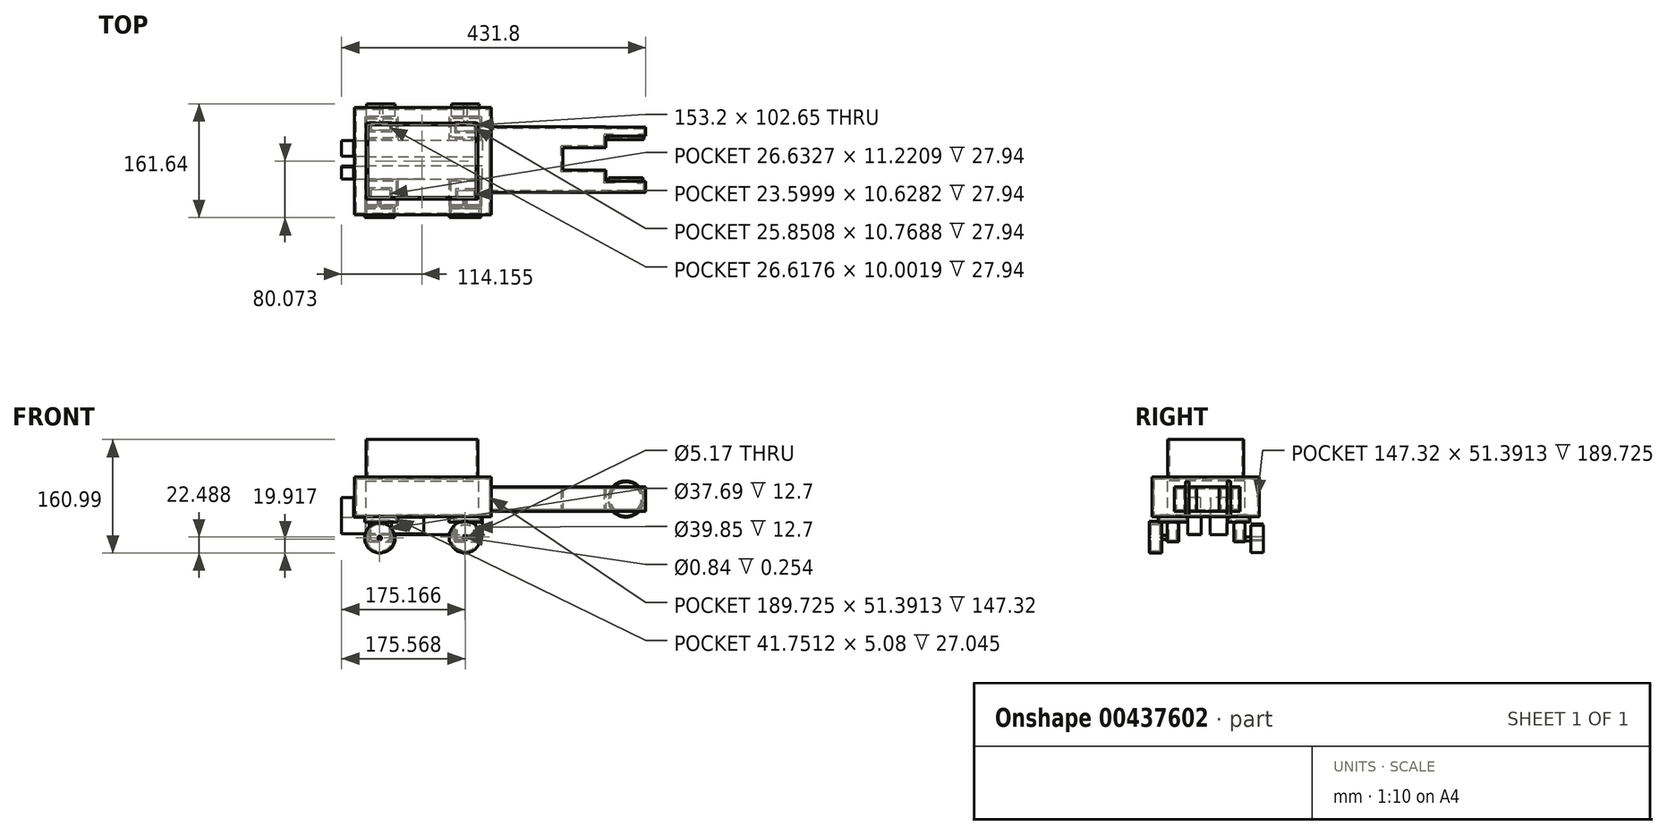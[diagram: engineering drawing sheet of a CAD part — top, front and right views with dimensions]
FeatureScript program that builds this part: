
annotation { "Feature Type Name" : "Feature", "Feature Type Description" : "" }
export const myFeature = defineFeature(function(context is Context, id is Id, definition is map)
    precondition{}
    {
        {
            var Q0;
            Q0=qCreatedBy(makeId("Front.planeOp"),FACE);
            var sketch = newSketch(context, id + "F0", { "sketchPlane" : qUnion([Q0])});
            skLineSegment(sketch, "E0.bottom", {"start": v(-98.79, 0) * mm, "end": v(96.02, 0) * mm});
            skLineSegment(sketch, "E0.top", {"start": v(-98.79, -56.47) * mm, "end": v(96.02, -56.47) * mm});
            skLineSegment(sketch, "E0.left", {"start": v(-98.79, 0) * mm, "end": v(-98.79, -56.47) * mm});
            skLineSegment(sketch, "E0.right", {"start": v(96.02, 0) * mm, "end": v(96.02, -56.47) * mm});
            skSolve(sketch);
        }
        {
            var Q0;
            Q0 = qSketchRegion(id + "F0", true);
            extrude(context, id + "F1", {"entities" : qUnion([Q0]), "depth" : 76.2 * mm});
        }
        {
            var Q0;
            Q0=makeQuery(id+"F1.opExtrude","CAP_FACE",FACE,{"disambiguationData":[OSD([sQuery(id+"F0.wireOp",EDGE,"E0.bottom"),sQuery(id+"F0.wireOp",EDGE,"E0.top"),sQuery(id+"F0.wireOp",EDGE,"E0.left"),sQuery(id+"F0.wireOp",EDGE,"E0.right")])],"isStart":true});
            extrude(context, id + "F2", {"entities" : qUnion([Q0]), "operationType" : NewBodyOperationType.ADD, "depth" : 76.2 * mm});
        }
        {
            var Q0;
            {var subQ0=sQuery(id+"F0.wireOp",EDGE,"E0.top");Q0=makeQuery(id+"F2.boolean.opBoolean","MERGE",FACE,{"derivedFrom":[makeQuery(id+"F1.opExtrude","SWEPT_FACE",FACE,{"disambiguationData":[OSD([subQ0])]}),makeQuery(id+"F2.opExtrude","SWEPT_FACE",FACE,{"disambiguationData":[OSD([subQ0])]})]});}
            var sketch = newSketch(context, id + "F3", { "sketchPlane" : qUnion([Q0])});
            skSolve(sketch);
        }
        {
            var Q0;
            {var subQ0=sQuery(id+"F0.wireOp",EDGE,"E0.top");Q0=makeQuery(id+"F3.imprint","IMPRINT",FACE,{"disambiguationData":[TD([[makeQuery(id+"F3.imprint","IMPRINT",EDGE,{"derivedFrom":makeQuery(id+"F1.opExtrude","CAP_EDGE",EDGE,{"disambiguationData":[OSD([subQ0])],"isStart":false})}),-1.0]])]});}
            var sketch = newSketch(context, id + "F4", { "sketchPlane" : qUnion([Q0])});
            skLineSegment(sketch, "E1.bottom", {"start": v(81.5, -62.59) * mm, "end": v(35.53, -62.59) * mm});
            skLineSegment(sketch, "E1.top", {"start": v(81.5, -30.8) * mm, "end": v(35.53, -30.8) * mm});
            skLineSegment(sketch, "E1.left", {"start": v(81.5, -62.59) * mm, "end": v(81.5, -30.8) * mm});
            skLineSegment(sketch, "E1.right", {"start": v(35.53, -62.59) * mm, "end": v(35.53, -30.8) * mm});
            skLineSegment(sketch, "E2.bottom", {"start": v(-83.86, -62.59) * mm, "end": v(-37.03, -62.59) * mm});
            skLineSegment(sketch, "E2.top", {"start": v(-83.86, -30.8) * mm, "end": v(-37.03, -30.8) * mm});
            skLineSegment(sketch, "E2.left", {"start": v(-83.86, -62.59) * mm, "end": v(-83.86, -30.8) * mm});
            skLineSegment(sketch, "E2.right", {"start": v(-37.03, -62.59) * mm, "end": v(-37.03, -30.8) * mm});
            skLineSegment(sketch, "E3.bottom", {"start": v(-83.86, 25.2) * mm, "end": v(-37.03, 25.2) * mm});
            skLineSegment(sketch, "E3.top", {"start": v(-83.86, 67.3) * mm, "end": v(-37.03, 67.3) * mm});
            skLineSegment(sketch, "E3.left", {"start": v(-83.86, 25.2) * mm, "end": v(-83.86, 67.3) * mm});
            skLineSegment(sketch, "E3.right", {"start": v(-37.03, 25.2) * mm, "end": v(-37.03, 67.3) * mm});
            skLineSegment(sketch, "E4.bottom", {"start": v(35.53, 25.2) * mm, "end": v(81.5, 25.2) * mm});
            skLineSegment(sketch, "E4.top", {"start": v(35.53, 67.3) * mm, "end": v(81.5, 67.3) * mm});
            skLineSegment(sketch, "E4.left", {"start": v(35.53, 25.2) * mm, "end": v(35.53, 67.3) * mm});
            skLineSegment(sketch, "E4.right", {"start": v(81.5, 25.2) * mm, "end": v(81.5, 67.3) * mm});
            skSolve(sketch);
        }
        {
            var Q0;
            Q0 = qSketchRegion(id + "F4", true);
            extrude(context, id + "F5", {"entities" : qUnion([Q0]), "operationType" : NewBodyOperationType.ADD, "depth" : 7.62 * mm});
        }
        {
            var Q0;
            {var subQ0=sQuery(id+"F0.wireOp",EDGE,"E0.top");Q0=makeQuery(id+"F3.imprint","IMPRINT",FACE,{"disambiguationData":[TD([[makeQuery(id+"F3.imprint","IMPRINT",EDGE,{"derivedFrom":makeQuery(id+"F1.opExtrude","CAP_EDGE",EDGE,{"disambiguationData":[OSD([subQ0])],"isStart":false})}),-1.0]])]});}
            var sketch = newSketch(context, id + "F6", { "sketchPlane" : qUnion([Q0])});
            skLineSegment(sketch, "E5.bottom", {"start": v(-77.55, 54.61) * mm, "end": v(-45.84, 54.61) * mm});
            skLineSegment(sketch, "E5.top", {"start": v(-77.55, 38.31) * mm, "end": v(-45.84, 38.31) * mm});
            skLineSegment(sketch, "E5.left", {"start": v(-77.55, 54.61) * mm, "end": v(-77.55, 38.31) * mm});
            skLineSegment(sketch, "E5.right", {"start": v(-45.84, 54.61) * mm, "end": v(-45.84, 38.31) * mm});
            skLineSegment(sketch, "E6.bottom", {"start": v(44.62, 54.91) * mm, "end": v(73.3, 54.91) * mm});
            skLineSegment(sketch, "E6.top", {"start": v(44.62, 39.2) * mm, "end": v(73.3, 39.2) * mm});
            skLineSegment(sketch, "E6.left", {"start": v(44.62, 54.91) * mm, "end": v(44.62, 39.2) * mm});
            skLineSegment(sketch, "E6.right", {"start": v(73.3, 54.91) * mm, "end": v(73.3, 39.2) * mm});
            skLineSegment(sketch, "E7.bottom", {"start": v(43.35, -39.87) * mm, "end": v(74.28, -39.87) * mm});
            skLineSegment(sketch, "E7.top", {"start": v(43.35, -55.72) * mm, "end": v(74.28, -55.72) * mm});
            skLineSegment(sketch, "E7.left", {"start": v(43.35, -39.87) * mm, "end": v(43.35, -55.72) * mm});
            skLineSegment(sketch, "E7.right", {"start": v(74.28, -39.87) * mm, "end": v(74.28, -55.72) * mm});
            skLineSegment(sketch, "E8.bottom", {"start": v(-77.57, -40.9) * mm, "end": v(-45.87, -40.9) * mm});
            skLineSegment(sketch, "E8.top", {"start": v(-77.57, -55.97) * mm, "end": v(-45.87, -55.97) * mm});
            skLineSegment(sketch, "E8.left", {"start": v(-77.57, -40.9) * mm, "end": v(-77.57, -55.97) * mm});
            skLineSegment(sketch, "E8.right", {"start": v(-45.87, -40.9) * mm, "end": v(-45.87, -55.97) * mm});
            skSolve(sketch);
        }
        {
            var Q0;
            Q0 = qSketchRegion(id + "F6", true);
            extrude(context, id + "F7", {"entities" : qUnion([Q0]), "operationType" : NewBodyOperationType.ADD, "depth" : 35.56 * mm});
        }
        {
            var Q0;
            Q0=makeQuery(id+"F7.opExtrude","SWEPT_FACE",FACE,{"disambiguationData":[OSD([sQuery(id+"F6.wireOp",EDGE,"E8.top")])]});
            var sketch = newSketch(context, id + "F8", { "sketchPlane" : qUnion([Q0])});
            skCircle(sketch, "E9", {"center": v(61, -87.01) * mm, "radius": 2.29 * mm});
            skPoint(sketch, "E9.first.point", {"position": v(59.2, -85.58) * mm});
            skPoint(sketch, "E9.second.point", {"position": v(62.7, -88.54) * mm});
            skPoint(sketch, "E9.third.point", {"position": v(60, -89.08) * mm});
            skCircle(sketch, "E10", {"center": v(-58.73, -87.73) * mm, "radius": 2.59 * mm});
            skPoint(sketch, "E10.first.point", {"position": v(-61.08, -86.66) * mm});
            skPoint(sketch, "E10.second.point", {"position": v(-56.52, -89.08) * mm});
            skPoint(sketch, "E10.third.point", {"position": v(-61.08, -88.8) * mm});
            skSolve(sketch);
        }
        {
            var Q0;
            Q0 = qSketchRegion(id + "F8", true);
            extrude(context, id + "F9", {"entities" : qUnion([Q0]), "operationType" : NewBodyOperationType.ADD, "depth" : 25.4 * mm});
        }
        {
            var Q0;
            Q0=makeQuery(id+"F9.opExtrude","CAP_FACE",FACE,{"disambiguationData":[OSD([sQuery(id+"F8.wireOp",EDGE,"E10")])],"isStart":false});
            var sketch = newSketch(context, id + "F10", { "sketchPlane" : qUnion([Q0])});
            skCircle(sketch, "E11", {"center": v(-58.73, -87.73) * mm, "radius": 19.64 * mm});
            skCircle(sketch, "E12", {"center": v(60.96, -86.76) * mm, "radius": 20.44 * mm});
            skSolve(sketch);
        }
        {
            var Q0;
            Q0=makeQuery(id+"F10.imprint","IMPRINT",FACE,{"disambiguationData":[TD([[makeQuery(id+"F10.imprint","IMPRINT",EDGE,{"derivedFrom":sQuery(id+"F10.wireOp",EDGE,"E11")}),1.0]])]});
            var Q1;
            Q1=makeQuery(id+"F10.imprint","IMPRINT",FACE,{"disambiguationData":[TD([[makeQuery(id+"F10.imprint","IMPRINT",EDGE,{"derivedFrom":sQuery(id+"F10.wireOp",EDGE,"E12")}),1.0]])]});
            extrude(context, id + "F11", {"entities" : qUnion([Q0, Q1]), "oppositeDirection" : true, "depth" : 17.78 * mm});
        }
        {
            var Q0;
            Q0=makeQuery(id+"F7.opExtrude","SWEPT_FACE",FACE,{"disambiguationData":[OSD([sQuery(id+"F6.wireOp",EDGE,"E5.bottom")])]});
            var sketch = newSketch(context, id + "F12", { "sketchPlane" : qUnion([Q0])});
            skCircle(sketch, "E13", {"center": v(-62.91, -86.26) * mm, "radius": 2.57 * mm});
            skCircle(sketch, "E14", {"center": v(58.61, -85.53) * mm, "radius": 2.96 * mm});
            skSolve(sketch);
        }
        {
            var Q0;
            Q0 = qSketchRegion(id + "F12", true);
            extrude(context, id + "F13", {"entities" : qUnion([Q0]), "operationType" : NewBodyOperationType.ADD, "depth" : 25.4 * mm});
        }
        {
            var Q0;
            Q0=makeQuery(id+"F13.opExtrude","CAP_FACE",FACE,{"disambiguationData":[OSD([sQuery(id+"F12.wireOp",EDGE,"E13")])],"isStart":false});
            var sketch = newSketch(context, id + "F14", { "sketchPlane" : qUnion([Q0])});
            skCircle(sketch, "E15", {"center": v(-62.91, -86.26) * mm, "radius": 21.39 * mm});
            skCircle(sketch, "E16", {"center": v(58.33, -85.16) * mm, "radius": 22.47 * mm});
            skSolve(sketch);
        }
        {
            var Q0;
            Q0 = qSketchRegion(id + "F14", true);
            extrude(context, id + "F15", {"entities" : qUnion([Q0]), "operationType" : NewBodyOperationType.ADD, "oppositeDirection" : true, "depth" : 17.78 * mm});
        }
        {
            var Q0;
            Q0 = qSketchRegion(id + "F12", true);
            extrude(context, id + "F16", {"entities" : qUnion([Q0]), "operationType" : NewBodyOperationType.ADD, "depth" : 25.65 * mm});
        }
        {
            var Q0;
            {var subQ0=sQuery(id+"F0.wireOp",EDGE,"E0.right");Q0=makeQuery(id+"F2.boolean.opBoolean","MERGE",FACE,{"derivedFrom":[makeQuery(id+"F1.opExtrude","SWEPT_FACE",FACE,{"disambiguationData":[OSD([subQ0])]}),makeQuery(id+"F2.opExtrude","SWEPT_FACE",FACE,{"disambiguationData":[OSD([subQ0])]})]});}
            var sketch = newSketch(context, id + "F17", { "sketchPlane" : qUnion([Q0])});
            skLineSegment(sketch, "E17.bottom", {"start": v(-44.5, -13.84) * mm, "end": v(48.96, -13.84) * mm});
            skLineSegment(sketch, "E17.top", {"start": v(-44.5, -48.37) * mm, "end": v(48.96, -48.37) * mm});
            skLineSegment(sketch, "E17.left", {"start": v(-44.5, -13.84) * mm, "end": v(-44.5, -48.37) * mm});
            skLineSegment(sketch, "E17.right", {"start": v(48.96, -13.84) * mm, "end": v(48.96, -48.37) * mm});
            skSolve(sketch);
        }
        {
            var Q0;
            Q0 = qSketchRegion(id + "F17", true);
            extrude(context, id + "F18", {"entities" : qUnion([Q0]), "operationType" : NewBodyOperationType.ADD, "depth" : 101.6 * mm});
        }
        {
            var Q0;
            Q0=makeQuery(id+"F18.opExtrude","CAP_FACE",FACE,{"disambiguationData":[OSD([sQuery(id+"F17.wireOp",EDGE,"E17.bottom"),sQuery(id+"F17.wireOp",EDGE,"E17.top"),sQuery(id+"F17.wireOp",EDGE,"E17.left"),sQuery(id+"F17.wireOp",EDGE,"E17.right")])],"isStart":false});
            var sketch = newSketch(context, id + "F19", { "sketchPlane" : qUnion([Q0])});
            skLineSegment(sketch, "E18.bottom", {"start": v(-44.5, -13.84) * mm, "end": v(-13.07, -13.84) * mm});
            skLineSegment(sketch, "E18.top", {"start": v(-44.5, -48.37) * mm, "end": v(-13.07, -48.37) * mm});
            skLineSegment(sketch, "E18.left", {"start": v(-44.5, -13.84) * mm, "end": v(-44.5, -48.37) * mm});
            skLineSegment(sketch, "E18.right", {"start": v(-13.07, -13.84) * mm, "end": v(-13.07, -48.37) * mm});
            skLineSegment(sketch, "E19.bottom", {"start": v(48.96, -13.84) * mm, "end": v(19.02, -13.84) * mm});
            skLineSegment(sketch, "E19.top", {"start": v(48.96, -48.37) * mm, "end": v(19.02, -48.37) * mm});
            skLineSegment(sketch, "E19.left", {"start": v(48.96, -13.84) * mm, "end": v(48.96, -48.37) * mm});
            skLineSegment(sketch, "E19.right", {"start": v(19.02, -13.84) * mm, "end": v(19.02, -48.37) * mm});
            skSolve(sketch);
        }
        {
            var Q0;
            Q0 = qSketchRegion(id + "F19", true);
            extrude(context, id + "F20", {"entities" : qUnion([Q0]), "operationType" : NewBodyOperationType.ADD, "depth" : 60.96 * mm});
        }
        {
            var Q0;
            Q0=makeQuery(id+"F20.opExtrude","CAP_FACE",FACE,{"disambiguationData":[OSD([sQuery(id+"F19.wireOp",EDGE,"E18.bottom"),sQuery(id+"F19.wireOp",EDGE,"E18.top"),sQuery(id+"F19.wireOp",EDGE,"E18.left"),sQuery(id+"F19.wireOp",EDGE,"E18.right")])],"isStart":false});
            var sketch = newSketch(context, id + "F21", { "sketchPlane" : qUnion([Q0])});
            skLineSegment(sketch, "E20.bottom", {"start": v(-44.5, -13.84) * mm, "end": v(-28.78, -13.84) * mm});
            skLineSegment(sketch, "E20.top", {"start": v(-44.5, -48.37) * mm, "end": v(-28.78, -48.37) * mm});
            skLineSegment(sketch, "E20.left", {"start": v(-44.5, -13.84) * mm, "end": v(-44.5, -48.37) * mm});
            skLineSegment(sketch, "E20.right", {"start": v(-28.78, -13.84) * mm, "end": v(-28.78, -48.37) * mm});
            skLineSegment(sketch, "E21.bottom", {"start": v(48.12, -13.84) * mm, "end": v(35.25, -13.84) * mm});
            skLineSegment(sketch, "E21.top", {"start": v(48.12, -48.37) * mm, "end": v(35.25, -48.37) * mm});
            skLineSegment(sketch, "E21.left", {"start": v(48.12, -13.84) * mm, "end": v(48.12, -48.37) * mm});
            skLineSegment(sketch, "E21.right", {"start": v(35.25, -13.84) * mm, "end": v(35.25, -48.37) * mm});
            skSolve(sketch);
        }
        {
            var Q0;
            Q0=makeQuery(id+"F21.imprint","IMPRINT",FACE,{"disambiguationData":[TD([[makeQuery(id+"F21.imprint","IMPRINT",EDGE,{"derivedFrom":sQuery(id+"F21.wireOp",EDGE,"E21.bottom")}),1.0]])]});
            var Q1;
            Q1=makeQuery(id+"F21.imprint","IMPRINT",FACE,{"disambiguationData":[TD([[makeQuery(id+"F21.imprint","IMPRINT",EDGE,{"derivedFrom":sQuery(id+"F21.wireOp",EDGE,"E20.bottom")}),-1.0]])]});
            extrude(context, id + "F22", {"entities" : qUnion([Q0, Q1]), "operationType" : NewBodyOperationType.ADD, "depth" : 56.4 * mm});
        }
        {
            var Q0;
            Q0=makeQuery(id+"F22.opExtrude","SWEPT_FACE",FACE,{"disambiguationData":[OSD([sQuery(id+"F21.wireOp",EDGE,"E20.right")])]});
            var sketch = newSketch(context, id + "F23", { "sketchPlane" : qUnion([Q0])});
            skCircle(sketch, "E22", {"center": v(-286.77, -31.1) * mm, "radius": 24.45 * mm});
            skPoint(sketch, "E22.centerSnap0", {"position": v(-258.58, -31.1) * mm});
            skPoint(sketch, "E22.centerSnap1", {"position": v(-286.77, -48.37) * mm});
            skSolve(sketch);
        }
        {
            var Q0;
            Q0 = qSketchRegion(id + "F23", true);
            extrude(context, id + "F24", {"entities" : qUnion([Q0]), "operationType" : NewBodyOperationType.ADD, "depth" : 5.08 * mm});
        }
        {
            var Q0;
            Q0=makeQuery(id+"F22.opExtrude","SWEPT_FACE",FACE,{"disambiguationData":[OSD([sQuery(id+"F21.wireOp",EDGE,"E21.right")])]});
            var sketch = newSketch(context, id + "F25", { "sketchPlane" : qUnion([Q0])});
            skCircle(sketch, "E23", {"center": v(286.77, -31.1) * mm, "radius": 25.74 * mm});
            skPoint(sketch, "E23.centerSnap0", {"position": v(314.96, -31.1) * mm});
            skPoint(sketch, "E23.centerSnap1", {"position": v(286.77, -13.84) * mm});
            skSolve(sketch);
        }
        {
            var Q0;
            Q0 = qSketchRegion(id + "F25", true);
            extrude(context, id + "F26", {"entities" : qUnion([Q0]), "operationType" : NewBodyOperationType.ADD, "depth" : 5.08 * mm});
        }
        {
            var Q0;
            {var subQ0=sQuery(id+"F0.wireOp",EDGE,"E0.bottom");Q0=makeQuery(id+"F2.boolean.opBoolean","MERGE",FACE,{"derivedFrom":[makeQuery(id+"F1.opExtrude","SWEPT_FACE",FACE,{"disambiguationData":[OSD([subQ0])]}),makeQuery(id+"F2.opExtrude","SWEPT_FACE",FACE,{"disambiguationData":[OSD([subQ0])]})]});}
            var sketch = newSketch(context, id + "F27", { "sketchPlane" : qUnion([Q0])});
            skLineSegment(sketch, "E24.bottom", {"start": v(-81.83, -54.06) * mm, "end": v(76.46, -54.06) * mm});
            skLineSegment(sketch, "E24.top", {"start": v(-81.83, 53.67) * mm, "end": v(76.46, 53.67) * mm});
            skLineSegment(sketch, "E24.left", {"start": v(-81.83, -54.06) * mm, "end": v(-81.83, 53.67) * mm});
            skLineSegment(sketch, "E24.right", {"start": v(76.46, -54.06) * mm, "end": v(76.46, 53.67) * mm});
            skSolve(sketch);
        }
        {
            var Q0;
            Q0 = qSketchRegion(id + "F27", true);
            extrude(context, id + "F28", {"entities" : qUnion([Q0]), "operationType" : NewBodyOperationType.ADD, "depth" : 53.34 * mm});
        }
        {
            var Q0;
            Q0=makeQuery(id+"F28.opExtrude","CAP_FACE",FACE,{"disambiguationData":[OSD([sQuery(id+"F27.wireOp",EDGE,"E24.bottom"),sQuery(id+"F27.wireOp",EDGE,"E24.top"),sQuery(id+"F27.wireOp",EDGE,"E24.left"),sQuery(id+"F27.wireOp",EDGE,"E24.right")])],"isStart":false});
            shell(context, id + "F29", {"entities" : qUnion([Q0]), "thickness" : 2.54 * mm});
        }
        {
            var Q0;
            Q0=makeQuery(id+"F6.imprint","IMPRINT",FACE,{"disambiguationData":[TD([[makeQuery(id+"F6.imprint","IMPRINT",EDGE,{"derivedFrom":sQuery(id+"F6.wireOp",EDGE,"E5.bottom")}),1.0]])]});
            var sketch = newSketch(context, id + "F30", { "sketchPlane" : qUnion([Q0])});
            skLineSegment(sketch, "E25.bottom", {"start": v(-82.68, -54.77) * mm, "end": v(77.16, -54.77) * mm});
            skLineSegment(sketch, "E25.top", {"start": v(-82.68, 54.78) * mm, "end": v(77.16, 54.78) * mm});
            skLineSegment(sketch, "E25.left", {"start": v(-82.68, -54.77) * mm, "end": v(-82.68, 54.78) * mm});
            skLineSegment(sketch, "E25.right", {"start": v(77.16, -54.77) * mm, "end": v(77.16, 54.78) * mm});
            skSolve(sketch);
        }
        {
            var Q0;
            Q0 = qSketchRegion(id + "F30", true);
            extrude(context, id + "F31", {"entities" : qUnion([Q0]), "operationType" : NewBodyOperationType.ADD, "oppositeDirection" : true, "depth" : 50.8 * mm});
        }
        {
            var Q0;
            Q0=makeQuery(id+"F6.imprint","IMPRINT",FACE,{"disambiguationData":[TD([[makeQuery(id+"F6.imprint","IMPRINT",EDGE,{"derivedFrom":sQuery(id+"F6.wireOp",EDGE,"E5.bottom")}),1.0]])]});
            var sketch = newSketch(context, id + "F32", { "sketchPlane" : qUnion([Q0])});
            skLineSegment(sketch, "E26.bottom", {"start": v(-82.59, -30) * mm, "end": v(82.82, -30) * mm});
            skLineSegment(sketch, "E26.top", {"start": v(-82.59, -6.2) * mm, "end": v(82.82, -6.2) * mm});
            skLineSegment(sketch, "E26.left", {"start": v(-82.59, -30) * mm, "end": v(-82.59, -6.2) * mm});
            skLineSegment(sketch, "E26.right", {"start": v(82.82, -30) * mm, "end": v(82.82, -6.2) * mm});
            skLineSegment(sketch, "E27.bottom", {"start": v(-82.18, 25.4) * mm, "end": v(82.82, 25.4) * mm});
            skLineSegment(sketch, "E27.top", {"start": v(-82.18, 6.53) * mm, "end": v(82.82, 6.53) * mm});
            skLineSegment(sketch, "E27.left", {"start": v(-82.18, 25.4) * mm, "end": v(-82.18, 6.53) * mm});
            skLineSegment(sketch, "E27.right", {"start": v(82.82, 25.4) * mm, "end": v(82.82, 6.53) * mm});
            skSolve(sketch);
        }
        {
            var Q0;
            Q0 = qSketchRegion(id + "F32", true);
            extrude(context, id + "F33", {"entities" : qUnion([Q0]), "operationType" : NewBodyOperationType.ADD, "depth" : 25.4 * mm});
        }
        {
            var Q0;
            Q0=qCreatedBy(makeId("Right.planeOp"),FACE);
            var sketch = newSketch(context, id + "F34", { "sketchPlane" : qUnion([Q0])});
            skLineSegment(sketch, "E28.bottom", {"start": v(29.1, -80.68) * mm, "end": v(6.76, -80.68) * mm});
            skLineSegment(sketch, "E28.top", {"start": v(29.1, -56.69) * mm, "end": v(6.76, -56.69) * mm});
            skLineSegment(sketch, "E28.left", {"start": v(29.1, -80.68) * mm, "end": v(29.1, -56.69) * mm});
            skLineSegment(sketch, "E28.right", {"start": v(6.76, -80.68) * mm, "end": v(6.76, -56.69) * mm});
            skLineSegment(sketch, "E29.bottom", {"start": v(-7.3, -80.68) * mm, "end": v(-25.51, -80.68) * mm});
            skLineSegment(sketch, "E29.top", {"start": v(-7.3, -56.69) * mm, "end": v(-25.51, -56.69) * mm});
            skLineSegment(sketch, "E29.left", {"start": v(-7.3, -80.68) * mm, "end": v(-7.3, -56.69) * mm});
            skLineSegment(sketch, "E29.right", {"start": v(-25.51, -80.68) * mm, "end": v(-25.51, -56.69) * mm});
            skSolve(sketch);
        }
        {
            var Q0;
            Q0 = qSketchRegion(id + "F34", true);
            extrude(context, id + "F35", {"entities" : qUnion([Q0]), "operationType" : NewBodyOperationType.ADD, "oppositeDirection" : true, "depth" : 116.84 * mm});
        }
        {
            var Q0;
            Q0=makeQuery(id+"F35.opExtrude","SWEPT_FACE",FACE,{"disambiguationData":[OSD([sQuery(id+"F34.wireOp",EDGE,"E28.top")])]});
            var sketch = newSketch(context, id + "F36", { "sketchPlane" : qUnion([Q0])});
            skLineSegment(sketch, "E30.bottom", {"start": v(-116.84, 29.1) * mm, "end": v(-99.71, 29.1) * mm});
            skLineSegment(sketch, "E30.top", {"start": v(-116.84, 6.76) * mm, "end": v(-99.71, 6.76) * mm});
            skLineSegment(sketch, "E30.left", {"start": v(-116.84, 29.1) * mm, "end": v(-116.84, 6.76) * mm});
            skLineSegment(sketch, "E30.right", {"start": v(-99.71, 29.1) * mm, "end": v(-99.71, 6.76) * mm});
            skLineSegment(sketch, "E31.bottom", {"start": v(-116.84, -8.14) * mm, "end": v(-99.71, -8.14) * mm});
            skLineSegment(sketch, "E31.top", {"start": v(-116.84, -25.51) * mm, "end": v(-99.71, -25.51) * mm});
            skLineSegment(sketch, "E31.left", {"start": v(-116.84, -8.14) * mm, "end": v(-116.84, -25.51) * mm});
            skLineSegment(sketch, "E31.right", {"start": v(-99.71, -8.14) * mm, "end": v(-99.71, -25.51) * mm});
            skSolve(sketch);
        }
        {
            var Q0;
            Q0 = qSketchRegion(id + "F36", true);
            extrude(context, id + "F37", {"entities" : qUnion([Q0]), "operationType" : NewBodyOperationType.ADD, "depth" : 27.94 * mm});
        }
    });
